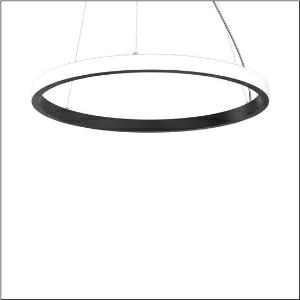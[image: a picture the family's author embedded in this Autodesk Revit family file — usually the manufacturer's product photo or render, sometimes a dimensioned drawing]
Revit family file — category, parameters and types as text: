
# Revit family: silica_r__21_ring-o_5pjbo4d1104a_942a
name_source: partatom
category: Lighting Fixtures
units: mm (PartAtom-declared; Revit-internal decimal feet)

## family parameters
Cut with Voids When Loaded = No
Host = Face
Light Source = No
Part Type = Normal
Room Calculation Point = No
Round Connector Dimension = Use Diameter
Shared = No

## types (1)
- Silica® 21 Ring-O (1 x LED, 8820 lm, 140 W, 3000K)
    Apparent Load = 140 VA
    CIE Flux Codes = 2 16 49 50 100
    Color Rendering = 80
    Color Temperature = 3000K
    Default Elevation = 1800 mm
    Description = Silica® 21 Ring-O, suspended luminaire, of PMMA, frosted, light emission: outer ring side luminous distribution, primary light characteristic: symmetric, installation type: suspended mounting, LED, rated luminous flux: 8.820lm, luminous efficacy: 63lm/W, light colour: 830, colour temperature: 3000K, with terminal, 5-pole, mains connection: 230V, AC/DC, 0/50..60Hz, rated input power: 140W, housing, of extruded aluminium section, jet black (RAL 9005), diameter: 1.480mm, ceiling canopy, jet black (RAL 9005), protection rating (lamp compartment): IP40, insulation class (complete): insulation class I (protective earthing), certification: CE, impact resistance: IK02, permissible operating ambient temperature: 0..+35°C, packaging unit: 1 piece
    Height = 48 mm  [stored 0.15748 ft]
    Lamp = 1 x LED
    Lamp Light Flux = 8820 lm
    Lamp Power = 140 W
    Lamp count = 1
    Length = 1480 mm
    Luminous efficacy = 63 lm/W
    Manufacturer = Siteco
    ModVariant = No
    Model = 5PJBO4D1104A
    Mounting Place = Ceiling
    Mounting Type = Pendant
    Number of Poles = 1
    OnlyDefault = Yes
    Power Factor = 1
    Product Name = Silica® 21 Ring-O
    Product group = suspended luminaire
    ProductGroupID = 904
    Protection Class = Protection class I
    Protection Degree = IP 40
    RLX_Detail_Level = 1
    RLX_Emergency_Light_Flux = 0 lm
    RLX_Emergency_Type = 0
    RLX_Emergency_Type_DB = No
    RlxData = <blob elided: 20533 chars, md5=697c9ffd>
    Socket = socket
    Standby Power = 0 W
    System Light Flux = 8820 lm
    System Power = 140 W
    Type Comments = Product without accessories
    Type Image = l_1258389.jpg
    URL = http://relux.com
    VarID = ---
    Voltage = 0 V
    Weight = 0.00 kg
    Width = 0 mm  [stored 0 ft]

note: [stored X ft] marks values corroborated as IEEE doubles in the binary element streams (Revit-internal decimal feet)

## geometry (parser evidence)
native form markers: Blend x4, Sweep x12
no freeform markers — native parametric forms only
